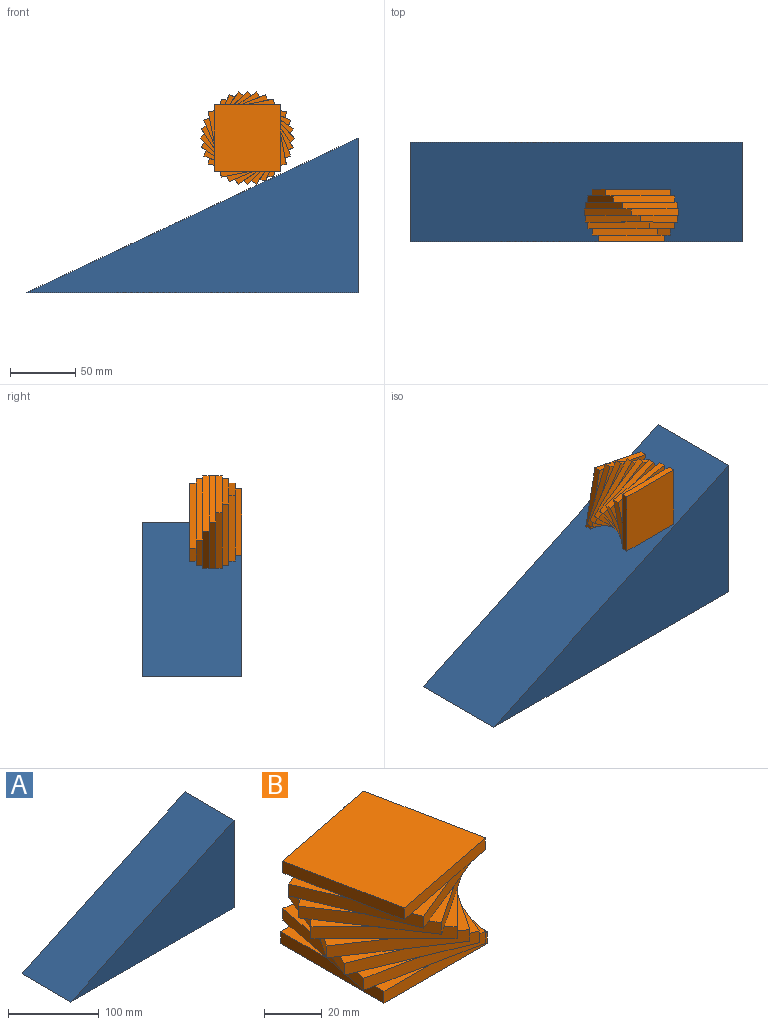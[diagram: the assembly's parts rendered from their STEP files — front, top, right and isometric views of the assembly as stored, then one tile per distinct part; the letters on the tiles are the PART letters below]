
ASSEMBLY  parts=2 mates=1
PART A: 5 faces, bbox 254x76.2x118.4 mm
  f0: plane 254x118.44mm, normal (-0.42,0,0.91), area 21355.7mm2, adj f1,f2,f3,f4
  f1: plane 254x76.2mm, normal (0,0,-1), area 19354.8mm2, adj f0,f2,f3,f4
  f2: plane 118.44x76.2mm, normal (1,0,0), area 9025.3mm2, adj f0,f1,f3,f4
  f3: plane 254x118.44mm, normal (0,-1,0), area 15042.2mm2, adj f0,f1,f2
  f4: plane 254x118.44mm, normal (0,1,0), area 15042.2mm2, adj f0,f1,f2
PART B: 90 faces, bbox 71.8x71.8x40 mm
  f0: plane 22.9x8.76mm, normal (0,0,1), area 52.1mm2, adj f75,f76,f84
  f1: plane 22.9x8.76mm, normal (0,0,1), area 52.1mm2, adj f75,f78,f87
  f2: plane 22.9x8.76mm, normal (0,0,1), area 52.1mm2, adj f77,f78,f86
  f3: plane 21.57x12.72mm, normal (0,0,1), area 52.1mm2, adj f66,f69,f75
  f4: plane 21.57x12.72mm, normal (0,0,1), area 52.1mm2, adj f68,f69,f78
  f5: plane 21.57x12.72mm, normal (0,0,1), area 52.1mm2, adj f67,f68,f77
  f6: plane 19.41x16.19mm, normal (0,0,1), area 52.1mm2, adj f57,f60,f66
  f7: plane 19.41x16.19mm, normal (0,0,1), area 52.1mm2, adj f59,f60,f69
  f8: plane 19.41x16.19mm, normal (0,0,1), area 52.1mm2, adj f58,f59,f68
  f9: plane 19.04x16.51mm, normal (0,0,1), area 52.1mm2, adj f48,f51,f57
  f10: plane 19.04x16.51mm, normal (0,0,1), area 52.1mm2, adj f50,f51,f60
  f11: plane 19.04x16.51mm, normal (0,0,1), area 52.1mm2, adj f49,f50,f59
  f12: plane 21.16x12.97mm, normal (0,0,1), area 52.1mm2, adj f39,f42,f48
  f13: plane 21.16x12.97mm, normal (0,0,1), area 52.1mm2, adj f41,f42,f51
  f14: plane 21.16x12.97mm, normal (0,0,1), area 52.1mm2, adj f40,f41,f50
  f15: plane 22.46x8.93mm, normal (0,0,1), area 52.1mm2, adj f30,f33,f39
  f16: plane 22.46x8.93mm, normal (0,0,1), area 52.1mm2, adj f32,f33,f42
  f17: plane 22.46x8.93mm, normal (0,0,1), area 52.1mm2, adj f31,f32,f41
  f18: plane 22.9x4.55mm, normal (0,0,1), area 52.1mm2, adj f21,f24,f30
  f19: plane 22.9x4.55mm, normal (0,0,1), area 52.1mm2, adj f23,f24,f33
  f20: plane 22.9x4.55mm, normal (0,0,1), area 52.1mm2, adj f22,f23,f32
  f21: plane 50.8x5mm, normal (1,0,0), area 254mm2, adj f18,f22,f24,f25,f26,f29
  f22: plane 50.8x5mm, normal (0,1,0), area 254mm2, adj f20,f21,f23,f25,f26,f27
  f23: plane 50.8x5mm, normal (-1,0,0), area 254mm2, adj f19,f20,f22,f24,f26,f28
  f24: plane 50.8x5mm, normal (0,-1,0), area 254mm2, adj f18,f19,f21,f23,f26,f35
  f25: plane 22.9x4.55mm, normal (0,0,1), area 52.1mm2, adj f21,f22,f31
  f26: plane 50.8x50.8mm, normal (0,0,-1), area 2580.6mm2, adj f21,f22,f23,f24
  f27: plane 23.35x4.47mm, normal (0,0,-1), area 52.1mm2, adj f22,f31,f32
  f28: plane 23.35x4.47mm, normal (0,0,-1), area 52.1mm2, adj f23,f32,f33
  f29: plane 23.35x4.47mm, normal (0,0,-1), area 52.1mm2, adj f21,f30,f31
  f30: plane 49.82x9.91mm, normal (0.98,-0.2,0), area 254mm2, adj f15,f18,f29,f31,f33,f34,f35,f38
  f31: plane 49.82x9.91mm, normal (0.2,0.98,0), area 254mm2, adj f17,f25,f27,f29,f30,f32,f34,f36
  f32: plane 49.82x9.91mm, normal (-0.98,0.2,0), area 254mm2, adj f16,f17,f20,f27,f28,f31,f33,f37
  f33: plane 49.82x9.91mm, normal (-0.2,-0.98,0), area 254mm2, adj f15,f16,f19,f28,f30,f32,f35,f44
  f34: plane 22.46x8.93mm, normal (0,0,1), area 52.1mm2, adj f30,f31,f40
  f35: plane 23.35x4.47mm, normal (0,0,-1), area 52.1mm2, adj f24,f30,f33
  f36: plane 22.9x8.76mm, normal (0,0,-1), area 52.1mm2, adj f31,f40,f41
  f37: plane 22.9x8.76mm, normal (0,0,-1), area 52.1mm2, adj f32,f41,f42
  f38: plane 22.9x8.76mm, normal (0,0,-1), area 52.1mm2, adj f30,f39,f40
  f39: plane 46.93x19.44mm, normal (0.92,-0.38,0), area 254mm2, adj f12,f15,f38,f40,f42,f43,f44,f47
  f40: plane 46.93x19.44mm, normal (0.38,0.92,0), area 254mm2, adj f14,f34,f36,f38,f39,f41,f43,f45
  f41: plane 46.93x19.44mm, normal (-0.92,0.38,0), area 254mm2, adj f13,f14,f17,f36,f37,f40,f42,f46
  f42: plane 46.93x19.44mm, normal (-0.38,-0.92,0), area 254mm2, adj f12,f13,f16,f37,f39,f41,f44,f53
  f43: plane 21.16x12.97mm, normal (0,0,1), area 52.1mm2, adj f39,f40,f49
  f44: plane 22.9x8.76mm, normal (0,0,-1), area 52.1mm2, adj f33,f39,f42
  f45: plane 21.57x12.72mm, normal (0,0,-1), area 52.1mm2, adj f40,f49,f50
  f46: plane 21.57x12.72mm, normal (0,0,-1), area 52.1mm2, adj f41,f50,f51
  f47: plane 21.57x12.72mm, normal (0,0,-1), area 52.1mm2, adj f39,f48,f49
  f48: plane 42.24x28.22mm, normal (0.83,-0.56,0), area 254mm2, adj f9,f12,f47,f49,f51,f52,f53,f56
  f49: plane 42.24x28.22mm, normal (0.56,0.83,0), area 254mm2, adj f11,f43,f45,f47,f48,f50,f52,f54
  f50: plane 42.24x28.22mm, normal (-0.83,0.56,0), area 254mm2, adj f10,f11,f14,f45,f46,f49,f51,f55
  f51: plane 42.24x28.22mm, normal (-0.56,-0.83,0), area 254mm2, adj f9,f10,f13,f46,f48,f50,f53,f62
  f52: plane 19.04x16.51mm, normal (0,0,1), area 52.1mm2, adj f48,f49,f58
  f53: plane 21.57x12.72mm, normal (0,0,-1), area 52.1mm2, adj f42,f48,f51
  f54: plane 19.41x16.19mm, normal (0,0,-1), area 52.1mm2, adj f49,f58,f59
  f55: plane 19.41x16.19mm, normal (0,0,-1), area 52.1mm2, adj f50,f59,f60
  f56: plane 19.41x16.19mm, normal (0,0,-1), area 52.1mm2, adj f48,f57,f58
  f57: plane 35.92x35.92mm, normal (0.71,-0.71,0), area 254mm2, adj f6,f9,f56,f58,f60,f61,f62,f65
  f58: plane 35.92x35.92mm, normal (0.71,0.71,0), area 254mm2, adj f8,f52,f54,f56,f57,f59,f61,f63
  f59: plane 35.92x35.92mm, normal (-0.71,0.71,0), area 254mm2, adj f7,f8,f11,f54,f55,f58,f60,f64
  f60: plane 35.92x35.92mm, normal (-0.71,-0.71,0), area 254mm2, adj f6,f7,f10,f55,f57,f59,f62,f71
  f61: plane 19.41x16.19mm, normal (0,0,1), area 52.1mm2, adj f57,f58,f67
  f62: plane 19.41x16.19mm, normal (0,0,-1), area 52.1mm2, adj f51,f57,f60
  f63: plane 19.04x16.51mm, normal (0,0,-1), area 52.1mm2, adj f58,f67,f68
  f64: plane 19.04x16.51mm, normal (0,0,-1), area 52.1mm2, adj f59,f68,f69
  f65: plane 19.04x16.51mm, normal (0,0,-1), area 52.1mm2, adj f57,f66,f67
  f66: plane 42.24x28.22mm, normal (0.56,-0.83,0), area 254mm2, adj f3,f6,f65,f67,f69,f70,f71,f74
  f67: plane 42.24x28.22mm, normal (0.83,0.56,0), area 254mm2, adj f5,f61,f63,f65,f66,f68,f70,f72
  f68: plane 42.24x28.22mm, normal (-0.56,0.83,0), area 254mm2, adj f4,f5,f8,f63,f64,f67,f69,f73
  f69: plane 42.24x28.22mm, normal (-0.83,-0.56,0), area 254mm2, adj f3,f4,f7,f64,f66,f68,f71,f80
  f70: plane 21.57x12.72mm, normal (0,0,1), area 52.1mm2, adj f66,f67,f76
  f71: plane 19.04x16.51mm, normal (0,0,-1), area 52.1mm2, adj f60,f66,f69
  f72: plane 21.16x12.97mm, normal (0,0,-1), area 52.1mm2, adj f67,f76,f77
  f73: plane 21.16x12.97mm, normal (0,0,-1), area 52.1mm2, adj f68,f77,f78
  f74: plane 21.16x12.97mm, normal (0,0,-1), area 52.1mm2, adj f66,f75,f76
  f75: plane 46.93x19.44mm, normal (0.38,-0.92,0), area 254mm2, adj f0,f1,f3,f74,f76,f78,f80,f83
  f76: plane 46.93x19.44mm, normal (0.92,0.38,0), area 254mm2, adj f0,f70,f72,f74,f75,f77,f79,f81
  f77: plane 46.93x19.44mm, normal (-0.38,0.92,0), area 254mm2, adj f2,f5,f72,f73,f76,f78,f79,f82
  f78: plane 46.93x19.44mm, normal (-0.92,-0.38,0), area 254mm2, adj f1,f2,f4,f73,f75,f77,f80,f89
  f79: plane 22.9x8.76mm, normal (0,0,1), area 52.1mm2, adj f76,f77,f85
  f80: plane 21.16x12.97mm, normal (0,0,-1), area 52.1mm2, adj f69,f75,f78
  f81: plane 22.46x8.93mm, normal (0,0,-1), area 52.1mm2, adj f76,f84,f85
  f82: plane 22.46x8.93mm, normal (0,0,-1), area 52.1mm2, adj f77,f85,f86
  f83: plane 22.46x8.93mm, normal (0,0,-1), area 52.1mm2, adj f75,f84,f87
  f84: plane 49.82x9.91mm, normal (0.98,0.2,0), area 254mm2, adj f0,f81,f83,f85,f87,f88
  f85: plane 49.82x9.91mm, normal (-0.2,0.98,0), area 254mm2, adj f79,f81,f82,f84,f86,f88
  f86: plane 49.82x9.91mm, normal (-0.98,-0.2,0), area 254mm2, adj f2,f82,f85,f87,f88,f89
  f87: plane 49.82x9.91mm, normal (0.2,-0.98,0), area 254mm2, adj f1,f83,f84,f86,f88,f89
  f88: plane 59.73x59.73mm, normal (0,0,1), area 2580.6mm2, adj f84,f85,f86,f87
  f89: plane 22.46x8.93mm, normal (0,0,-1), area 52.1mm2, adj f78,f86,f87
PLACE A t=(38.29,20.42,-30.51)mm
PLACE B rot(axis=(-1,0,0),90deg) t=(80.62,-17.68,87.97)mm
MATE parallel A.f3 <-> B.f26  axis (0,-1,0) through (80.62,-17.68,8.97)mm
